# Revit family: RN 26020 Rubinetto a sfera con volantino a farfalla
name_source: partatom
category: Rohrzubehör
units: mm (PartAtom-declared; Revit-internal decimal feet)

## family parameters
Arbeitsebenenbasiert = Nein
Beim Laden mit Abzugskörper schneiden = Nein
Bemaßung runder Anschluss = Durchmesser verwenden
Gemeinsam genutzt = Nein
Immer vertikal = Ja
Teiletyp = Ventil - Zerlegung in

## types (6) — shared parameters
1.010.00.2 Number of the part of the guideline = 2
1.010.00.3 Issue date (month) of the guideline = 201601
1.010.00.4 Manufacturer name = R. Nussbaum AG
1.010.00.5 Revision date of the file = 20190514
1.100.00.3 Sort number for display sequence = 4
1.100.00.4 Product designation = Absperr- und Regelarmaturen
1.960/3L.00.8 Link (URL) = https://www.nussbaum.ch
2.700.00.4 valve assembly type = 11
2.700.00.7 maximum operating temperature TB [°C] = 100
2.700.00.8 maximum operating pressure(working pressure) ps [1.0 · 102 Pa] = 16
Connector Visibility = Nein
EnclosingSpace Visibility = Nein
Hersteller = R. Nussbauzm AG
Modell = 0
URL = https://www.nussbaum.ch

## per-type parameters (varying)
| type | 1.800.00.3 BS number | 1.810.00.3 Manufacturer’s reference number | 1.810.00.4 DATANORM number | 1.810.00.5 StLB number | 1.810.00.6 GTIN number | 2.700.00.26 product description | 2.700.00.5 nominal size DN | 2.700.00.6 kvs-value [m3/h] | CONNECTOR0_DIAMETER_dX_0r | CONNECTOR0_dX_00 | CONNECTOR0_dX_01 | CONNECTOR0_ref_dX | CONNECTOR1_DIAMETER_dX_0r | CONNECTOR1_dX_00 | CONNECTOR1_dX_01 | CONNECTOR1_ref_dX | R. Nussbaum AG 26020.52 en Visibility | R. Nussbaum AG 26020.53 en Visibility | R. Nussbaum AG 26020.54 en Visibility | R. Nussbaum AG 26020.55 en Visibility | R. Nussbaum AG 26020.56 en Visibility | R. Nussbaum AG 26020.57 en Visibility | Typenkommentare |
| DN 8 | 0040070000000000000000000000010010000000000000000100000000 | 26020.52 | 26020.52 | 655.131 | 7612945676986 | 26020.52, Kugelhahn mit Flügelgriff, mit Innengewinde, DN=8, Rp=¼ | 8 | 8 | 8 mm  [stored 0.0262467 ft] | 23 mm  [stored 0.0754593 ft] | 11 mm  [stored 0.0360892 ft] | 11 mm  [stored 0.0360892 ft] | 8 mm  [stored 0.0262467 ft] | 11 mm  [stored 0.0360892 ft] | 23 mm  [stored 0.0754593 ft] | 11 mm  [stored 0.0360892 ft] | Ja | Nein | Nein | Nein | Nein | Nein | Valvola d'arrestoDN 8 |
| DN 10 | 0040070000000000000000000000010010000000000000000200000000 | 26020.53 | 26020.53 | 655.132 | 7612945677006 | 26020.53, Kugelhahn mit Flügelgriff, mit Innengewinde, DN=10, Rp=3/8 | 10 | 10.3 | 8 mm  [stored 0.0262467 ft] | 30 mm  [stored 0.0984252 ft] | 14 mm  [stored 0.0459318 ft] | 14 mm  [stored 0.0459318 ft] | 8 mm  [stored 0.0262467 ft] | 14 mm  [stored 0.0459318 ft] | 30 mm  [stored 0.0984252 ft] | 14 mm  [stored 0.0459318 ft] | Nein | Ja | Nein | Nein | Nein | Nein | Valvola d'arrestoDN 10 |
| DN 15 | 0040070000000000000000000000010010000000000000000300000000 | 26020.54 | 26020.54 | 655.133 | 7612945677020 | 26020.54, Kugelhahn mit Flügelgriff, mit Innengewinde, DN=15, Rp=½ | 15 | 35 | 15 mm  [stored 0.0492126 ft] | 38 mm | 18 mm | 18 mm | 15 mm  [stored 0.0492126 ft] | 18 mm | 38 mm | 18 mm | Nein | Nein | Ja | Nein | Nein | Nein | Valvola d'arrestoDN 15 |
| DN 20 | 0040070000000000000000000000010010000000000000000400000000 | 26020.55 | 26020.55 | 655.134 | 7612945677044 | 26020.55, Kugelhahn mit Flügelgriff, mit Innengewinde, DN=20, Rp=¾ | 20 | 47 | 20 mm | 40 mm | 20 mm | 20 mm | 20 mm | 20 mm | 40 mm | 20 mm | Nein | Nein | Nein | Ja | Nein | Nein | Valvola d'arrestoDN 20 |
| DN 25 | 0040070000000000000000000000010010000000000000000500000000 | 26020.56 | 26020.56 | 655.135 | 7612945677068 | 26020.56, Kugelhahn mit Flügelgriff, mit Innengewinde, DN=25, Rp=1 | 25 | 54 | 25 mm  [stored 0.082021 ft] | 45 mm | 23 mm  [stored 0.0754593 ft] | 23 mm  [stored 0.0754593 ft] | 25 mm  [stored 0.082021 ft] | 23 mm  [stored 0.0754593 ft] | 45 mm | 23 mm  [stored 0.0754593 ft] | Nein | Nein | Nein | Nein | Ja | Nein | Valvola d'arrestoDN 25 |
| DN 32 | 0040070000000000000000000000010010000000000000000600000000 | 26020.57 | 26020.57 |  | 7612945703446 | 26020.57, Kugelhahn mit Flügelgriff, mit Innengewinde, DN=32, Rp=1¼ | 32 | 82 | 32 mm | 55 mm | 30 mm  [stored 0.0984252 ft] | 30 mm  [stored 0.0984252 ft] | 32 mm | 30 mm  [stored 0.0984252 ft] | 55 mm | 30 mm  [stored 0.0984252 ft] | Nein | Nein | Nein | Nein | Nein | Ja | Valvola d'arrestoDN 32 |

note: [stored X ft] marks values corroborated as IEEE doubles in the binary element streams (Revit-internal decimal feet)

## geometry (parser evidence)
native form markers: Sweep x1
no freeform markers — native parametric forms only
